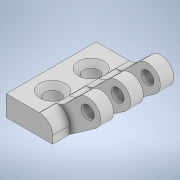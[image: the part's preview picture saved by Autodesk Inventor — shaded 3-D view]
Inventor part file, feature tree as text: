
AUTODESK INVENTOR PART (.ipt)
format: ipt  version: 2022 (Build 260153000, 153)  size: 199,168 bytes
history: native  units: mm
features: sketch x5, extrude x4, fillet x2, hole x1, pattern_linear x1
ambient origin geometry x8: Origin, YZ Plane, XZ Plane, XY Plane, X Axis, Y Axis, Z Axis, Center Point
bodies: Solid1 (feature_tree)
feature tree (13):
  extrude  "Extrusion1"  Depth=20.0mm
  extrude  "Extrusion2"  Depth=5.0mm
  extrude  "Extrusion3"  Depth=10.0mm
  hole  "Hole1"  [1 undecoded]
  fillet  "Fillet1"  Radius=10.0mm
  extrude  "Extrusion4"  Depth=5.0mm
  fillet  "Fillet2"  Radius=6.108652mm
  pattern_linear  "Rectangular Pattern1"  Spacing1=5.0mm  [1 undecoded]
  sketch  "Sketch2"  dims[d0=35.0mm d1=20.0mm]
  sketch  "Sketch3"  dims[d2=8.0mm d3=0.0mm d4=5.0mm]
  sketch  "Sketch4"  dims[d5=10.0mm d6=6.0mm]
  sketch  "Sketch5"  dims[d7=8.0mm d8=0.0mm d9=10.0mm d10=0.0mm d11=10.0mm]
  sketch  "Sketch6"  dims[d12=15.0mm d13=8.0mm d14=6.0mm d15=6.0mm d16=10.0mm d17=2.0mm d18=90.0deg d19=8.0mm d20=20.594885mm d21=6.108652mm d22=5.0mm d23=6.6mm d24=10.0mm d25=0.0mm d26=5.0mm d27=30.0mm d29=11.6mm]
note: 2 required parameter values undecoded (feature->parameter linkage not recoverable at this tier; creation-order binding heuristic only, values carry confidence <= 0.55)
